# Revit family: Shower-Valve_Trim-KOHLER-COMPOSED-K-73098T_1
name_source: partatom
category: Specialty Equipment
revit_build: Autodesk Revit 2017 (Build: 20160225_1515(x64)
units: mm (PartAtom-declared; Revit-internal decimal feet)

## family parameters
Cut with Voids When Loaded = No
Host = Face
OmniClass Number = 23.31.25.00
OmniClass Title = Toilet and Bath Specialties
Part Type = Normal
Room Calculation Point = No
Round Connector Dimension = Use Diameter
Shared = No

## types (3) — shared parameters
ADA Compliant = No
Assembly Code = C1030200
Date Modified = 10/06/2020
Default Elevation = 42"
Description = Modern Classic Single Control Rece. Shower only Trim
Handle Clearance = 2 15/16"
Height = 6 9/16"
Length = 3 7/16"
Manufacturer = KOHLER Co.
Master Format 2014 = 10 28 00
Master Format 2014 Name = Toilet, Bath, and Laundry Accessories
Material = Premium Metal Construction
Product Name = COMPOSED
URL = http://www.kohler.com.cn
WaterSense Certified = No
Width = 4 7/16"

## per-type parameters (varying)
| type | Finish | Model | Type |
| CP-Polished Chrome | Kohler-Metal-CP-Polished_Chrome | K-73098T-4-CP | 1 |
| AF-French Gold | Kohler-Metal-AF-Vibrant_French_Gold | K-73098T-4-AF | 2 |
| TT-Titanium Silver | Kohler-Metal-TT-Vibrant_Titanium | K-73098T-4-TT | 3 |

## geometry (parser evidence)
native form markers: Sweep x6
no freeform markers — native parametric forms only
